# Revit family: Basin-Semi-Recessed-Caroma Luna
name_source: partatom
category: Plumbing Fixtures
revit_build: Autodesk Revit 2014 (Build: 20140709_2115(x64)
units: mm (PartAtom-declared; Revit-internal decimal feet)

## types (2) — shared parameters
3 Tapholes = No
Assembly Code = D2010310
CW Connection = No
Depth_ANZRS = 153 mm  [stored 0.501969 ft]
Description = Caroma Luna Semi Recessed Basin
HW Connection = No
Keynote = WB
Length_ANZRS = 450 mm  [stored 1.47638 ft]
Manufacturer = GWA Bathrooms & Kitchens
Material_ANZRS = Porcelain-White-Caroma
ModifiedIssue_ANZRS = 20170210 $
Tap Penetrations = 100 mm  [stored 0.328084 ft]
Type Comments = Capacity: 4.8L to overflow, Overflow available only, Bracket included, White plug and chrome flush fitting waste included
URL = https://specify.caroma.com.au
Vent Connection = No
WFU = 2
Waste = Metal-Brass-Chrome
Waste Connection = Yes
Width_ANZRS = 380 mm
zero-valued in all types: Cost, Default Elevation

## per-type parameters (varying)
| type | 1 Taphole | Model | Spout Penetration |
| Luna Semi Recessed - 0 Tap Holes | No | 873605W | 100 mm  [stored 0.328084 ft] |
| Luna Semi Recessed - 1 Tap Holes | Yes | 873615W | 0 mm  [stored 0 ft] |

note: [stored X ft] marks values corroborated as IEEE doubles in the binary element streams (Revit-internal decimal feet)

## geometry (parser evidence)
native form markers: Blend x4, Sweep x1
no freeform markers — native parametric forms only
